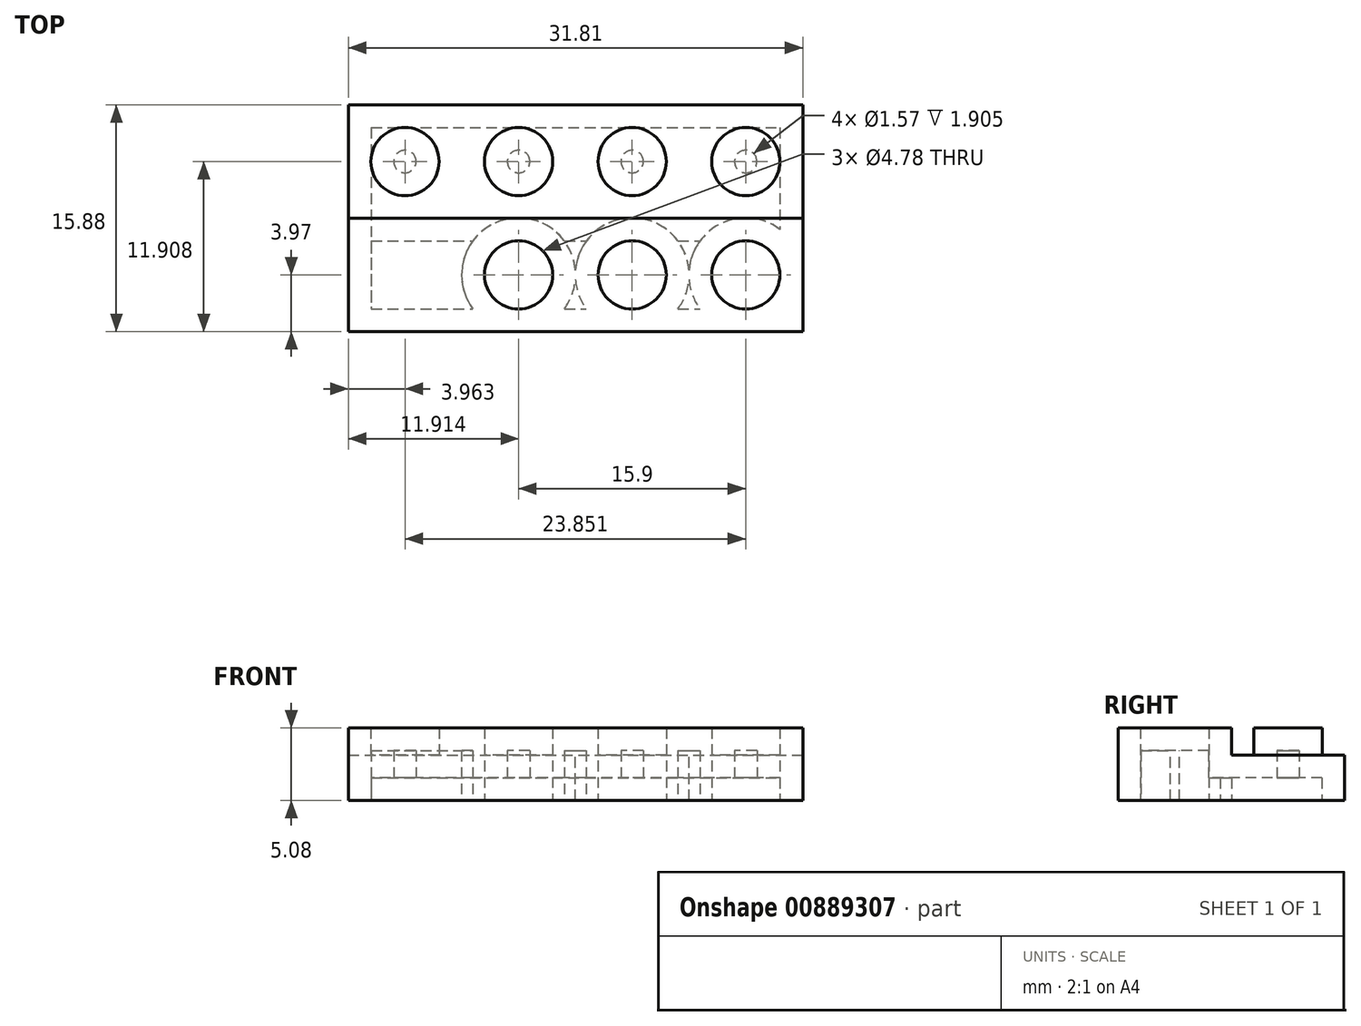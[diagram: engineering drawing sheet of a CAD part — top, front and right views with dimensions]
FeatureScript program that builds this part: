
annotation { "Feature Type Name" : "Feature", "Feature Type Description" : "" }
export const myFeature = defineFeature(function(context is Context, id is Id, definition is map)
    precondition{}
    {
        {
            var Q0;
            Q0=qCreatedBy(makeId("Top.planeOp"),FACE);
            var sketch = newSketch(context, id + "F0", { "sketchPlane" : qUnion([Q0])});
            skLineSegment(sketch, "E0.bottom", {"start": v(-38.8, 8.6) * mm, "end": v(-7, 8.6) * mm});
            skLineSegment(sketch, "E0.top", {"start": v(-38.8, -7.28) * mm, "end": v(-7, -7.28) * mm});
            skLineSegment(sketch, "E0.left", {"start": v(-38.8, 8.6) * mm, "end": v(-38.8, -7.28) * mm});
            skLineSegment(sketch, "E0.right", {"start": v(-7, 8.6) * mm, "end": v(-7, -7.28) * mm});
            skLineSegment(sketch, "E1", {"start": v(-38.8, 0.66) * mm, "end": v(-7, 0.66) * mm});
            skLineSegment(sketch, "E2", {"start": v(-7, 8.6) * mm, "end": v(-7, 0.66) * mm});
            skLineSegment(sketch, "E3", {"start": v(-7, 0.66) * mm, "end": v(-7, -7.28) * mm});
            skLineSegment(sketch, "E4", {"start": v(-38.8, 8.6) * mm, "end": v(-38.8, 0.66) * mm});
            skLineSegment(sketch, "E5", {"start": v(-38.8, -7.28) * mm, "end": v(-38.8, 0.66) * mm});
            skLineSegment(sketch, "E6", {"start": v(-7, -3.31) * mm, "end": v(-38.8, -3.31) * mm});
            skLineSegment(sketch, "E7", {"start": v(-38.8, -3.31) * mm, "end": v(-38.8, 4.63) * mm});
            skLineSegment(sketch, "E8", {"start": v(-38.8, 4.63) * mm, "end": v(-7, 4.63) * mm});
            skCircle(sketch, "E9", {"center": v(-34.85, 4.63) * mm, "radius": 2.39 * mm});
            skCircle(sketch, "E10.1.0.0", {"center": v(-26.9, 4.63) * mm, "radius": 2.39 * mm});
            skCircle(sketch, "E10.2.0.0", {"center": v(-18.95, 4.63) * mm, "radius": 2.39 * mm});
            skCircle(sketch, "E10.3.0.0", {"center": v(-11, 4.63) * mm, "radius": 2.39 * mm});
            skLineSegment(sketch, "E10.direction1", {"start": v(-34.85, 4.63) * mm, "end": v(-26.9, 4.63) * mm, "construction": true});
            skCircle(sketch, "E11.MirrorC", {"center": v(-34.85, -3.31) * mm, "radius": 2.39 * mm});
            skCircle(sketch, "E12.MirrorC", {"center": v(-26.9, -3.31) * mm, "radius": 2.39 * mm});
            skCircle(sketch, "E13.MirrorC", {"center": v(-18.95, -3.31) * mm, "radius": 2.39 * mm});
            skCircle(sketch, "E14.MirrorC", {"center": v(-11, -3.31) * mm, "radius": 2.39 * mm});
            skSolve(sketch);
        }
        {
            var Q0;
            {var subQ8=sQuery(id+"F0.wireOp",EDGE,"E0.bottom");Q0=makeQuery(id+"F0.imprint","IMPRINT",FACE,{"disambiguationData":[TD([[makeQuery(id+"F0.imprint","IMPRINT",EDGE,{"derivedFrom":subQ8}),-1.0]])]});}
            var Q1;
            {var subQ12=sQuery(id+"F0.wireOp",EDGE,"E1");Q1=makeQuery(id+"F0.imprint","IMPRINT",FACE,{"disambiguationData":[TD([[makeQuery(id+"F0.imprint","IMPRINT",EDGE,{"derivedFrom":subQ12}),1.0]])]});}
            var Q2;
            {var subQ12=sQuery(id+"F0.wireOp",EDGE,"E0.top");Q2=makeQuery(id+"F0.imprint","IMPRINT",FACE,{"disambiguationData":[TD([[makeQuery(id+"F0.imprint","IMPRINT",EDGE,{"derivedFrom":subQ12}),1.0]])]});}
            var Q3;
            {var subQ8=sQuery(id+"F0.wireOp",EDGE,"E1");Q3=makeQuery(id+"F0.imprint","IMPRINT",FACE,{"disambiguationData":[TD([[makeQuery(id+"F0.imprint","IMPRINT",EDGE,{"derivedFrom":subQ8}),-1.0]])]});}
            extrude(context, id + "F1", {"entities" : qUnion([Q0, Q1, Q2, Q3]), "depth" : 3.17 * mm, "offsetDistance" : 25.4 * mm});
        }
        {
            var Q0;
            {var subQ0=sQuery(id+"F0.wireOp",EDGE,"E9");var subQ1=sQuery(id+"F0.wireOp",EDGE,"E8");var subQ2=makeQuery(id+"F0.imprint","INTERSECT",VERTEX,{"disambiguationData":[OD(0.0)],"derivedFrom":[subQ1,subQ0]});Q0=makeQuery(id+"F0.imprint","IMPRINT",FACE,{"disambiguationData":[TD([[makeQuery(id+"F0.imprint","IMPRINT",EDGE,{"disambiguationData":[TD([[subQ2,-1.0]])],"derivedFrom":subQ1}),-1.0]])]});}
            var Q1;
            {var subQ0=sQuery(id+"F0.wireOp",EDGE,"E9");var subQ1=sQuery(id+"F0.wireOp",EDGE,"E8");var subQ2=makeQuery(id+"F0.imprint","INTERSECT",VERTEX,{"disambiguationData":[OD(0.0)],"derivedFrom":[subQ1,subQ0]});Q1=makeQuery(id+"F0.imprint","IMPRINT",FACE,{"disambiguationData":[TD([[makeQuery(id+"F0.imprint","IMPRINT",EDGE,{"disambiguationData":[TD([[subQ2,-1.0]])],"derivedFrom":subQ1}),1.0]])]});}
            var Q2;
            {var subQ0=sQuery(id+"F0.wireOp",EDGE,"E11.MirrorC");var subQ1=sQuery(id+"F0.wireOp",EDGE,"E6");var subQ2=makeQuery(id+"F0.imprint","INTERSECT",VERTEX,{"disambiguationData":[OD(0.0)],"derivedFrom":[subQ1,subQ0]});Q2=makeQuery(id+"F0.imprint","IMPRINT",FACE,{"disambiguationData":[TD([[makeQuery(id+"F0.imprint","IMPRINT",EDGE,{"disambiguationData":[TD([[subQ2,-1.0]])],"derivedFrom":subQ1}),-1.0]])]});}
            var Q3;
            {var subQ0=sQuery(id+"F0.wireOp",EDGE,"E11.MirrorC");var subQ1=sQuery(id+"F0.wireOp",EDGE,"E6");var subQ2=makeQuery(id+"F0.imprint","INTERSECT",VERTEX,{"disambiguationData":[OD(0.0)],"derivedFrom":[subQ1,subQ0]});Q3=makeQuery(id+"F0.imprint","IMPRINT",FACE,{"disambiguationData":[TD([[makeQuery(id+"F0.imprint","IMPRINT",EDGE,{"disambiguationData":[TD([[subQ2,-1.0]])],"derivedFrom":subQ1}),1.0]])]});}
            var Q4;
            {var subQ0=sQuery(id+"F0.wireOp",EDGE,"E12.MirrorC");var subQ1=sQuery(id+"F0.wireOp",EDGE,"E6");var subQ2=makeQuery(id+"F0.imprint","INTERSECT",VERTEX,{"disambiguationData":[OD(0.0)],"derivedFrom":[subQ1,subQ0]});Q4=makeQuery(id+"F0.imprint","IMPRINT",FACE,{"disambiguationData":[TD([[makeQuery(id+"F0.imprint","IMPRINT",EDGE,{"disambiguationData":[TD([[subQ2,-1.0]])],"derivedFrom":subQ1}),1.0]])]});}
            var Q5;
            {var subQ0=sQuery(id+"F0.wireOp",EDGE,"E12.MirrorC");var subQ1=sQuery(id+"F0.wireOp",EDGE,"E6");var subQ2=makeQuery(id+"F0.imprint","INTERSECT",VERTEX,{"disambiguationData":[OD(0.0)],"derivedFrom":[subQ1,subQ0]});Q5=makeQuery(id+"F0.imprint","IMPRINT",FACE,{"disambiguationData":[TD([[makeQuery(id+"F0.imprint","IMPRINT",EDGE,{"disambiguationData":[TD([[subQ2,-1.0]])],"derivedFrom":subQ1}),-1.0]])]});}
            var Q6;
            {var subQ0=sQuery(id+"F0.wireOp",EDGE,"E10.1.0.0");var subQ1=sQuery(id+"F0.wireOp",EDGE,"E8");var subQ2=makeQuery(id+"F0.imprint","INTERSECT",VERTEX,{"disambiguationData":[OD(0.0)],"derivedFrom":[subQ1,subQ0]});Q6=makeQuery(id+"F0.imprint","IMPRINT",FACE,{"disambiguationData":[TD([[makeQuery(id+"F0.imprint","IMPRINT",EDGE,{"disambiguationData":[TD([[subQ2,-1.0]])],"derivedFrom":subQ1}),-1.0]])]});}
            var Q7;
            {var subQ0=sQuery(id+"F0.wireOp",EDGE,"E10.1.0.0");var subQ1=sQuery(id+"F0.wireOp",EDGE,"E8");var subQ2=makeQuery(id+"F0.imprint","INTERSECT",VERTEX,{"disambiguationData":[OD(0.0)],"derivedFrom":[subQ1,subQ0]});Q7=makeQuery(id+"F0.imprint","IMPRINT",FACE,{"disambiguationData":[TD([[makeQuery(id+"F0.imprint","IMPRINT",EDGE,{"disambiguationData":[TD([[subQ2,-1.0]])],"derivedFrom":subQ1}),1.0]])]});}
            var Q8;
            {var subQ0=sQuery(id+"F0.wireOp",EDGE,"E13.MirrorC");var subQ1=sQuery(id+"F0.wireOp",EDGE,"E6");var subQ2=makeQuery(id+"F0.imprint","INTERSECT",VERTEX,{"disambiguationData":[OD(0.0)],"derivedFrom":[subQ1,subQ0]});Q8=makeQuery(id+"F0.imprint","IMPRINT",FACE,{"disambiguationData":[TD([[makeQuery(id+"F0.imprint","IMPRINT",EDGE,{"disambiguationData":[TD([[subQ2,-1.0]])],"derivedFrom":subQ1}),1.0]])]});}
            var Q9;
            {var subQ0=sQuery(id+"F0.wireOp",EDGE,"E13.MirrorC");var subQ1=sQuery(id+"F0.wireOp",EDGE,"E6");var subQ2=makeQuery(id+"F0.imprint","INTERSECT",VERTEX,{"disambiguationData":[OD(0.0)],"derivedFrom":[subQ1,subQ0]});Q9=makeQuery(id+"F0.imprint","IMPRINT",FACE,{"disambiguationData":[TD([[makeQuery(id+"F0.imprint","IMPRINT",EDGE,{"disambiguationData":[TD([[subQ2,-1.0]])],"derivedFrom":subQ1}),-1.0]])]});}
            var Q10;
            {var subQ0=sQuery(id+"F0.wireOp",EDGE,"E10.2.0.0");var subQ1=sQuery(id+"F0.wireOp",EDGE,"E8");var subQ2=makeQuery(id+"F0.imprint","INTERSECT",VERTEX,{"disambiguationData":[OD(0.0)],"derivedFrom":[subQ1,subQ0]});Q10=makeQuery(id+"F0.imprint","IMPRINT",FACE,{"disambiguationData":[TD([[makeQuery(id+"F0.imprint","IMPRINT",EDGE,{"disambiguationData":[TD([[subQ2,-1.0]])],"derivedFrom":subQ1}),1.0]])]});}
            var Q11;
            {var subQ0=sQuery(id+"F0.wireOp",EDGE,"E10.2.0.0");var subQ1=sQuery(id+"F0.wireOp",EDGE,"E8");var subQ2=makeQuery(id+"F0.imprint","INTERSECT",VERTEX,{"disambiguationData":[OD(0.0)],"derivedFrom":[subQ1,subQ0]});Q11=makeQuery(id+"F0.imprint","IMPRINT",FACE,{"disambiguationData":[TD([[makeQuery(id+"F0.imprint","IMPRINT",EDGE,{"disambiguationData":[TD([[subQ2,-1.0]])],"derivedFrom":subQ1}),-1.0]])]});}
            var Q12;
            {var subQ0=sQuery(id+"F0.wireOp",EDGE,"E14.MirrorC");var subQ1=sQuery(id+"F0.wireOp",EDGE,"E6");var subQ2=makeQuery(id+"F0.imprint","INTERSECT",VERTEX,{"disambiguationData":[OD(0.0)],"derivedFrom":[subQ1,subQ0]});Q12=makeQuery(id+"F0.imprint","IMPRINT",FACE,{"disambiguationData":[TD([[makeQuery(id+"F0.imprint","IMPRINT",EDGE,{"disambiguationData":[TD([[subQ2,-1.0]])],"derivedFrom":subQ1}),-1.0]])]});}
            var Q13;
            {var subQ0=sQuery(id+"F0.wireOp",EDGE,"E14.MirrorC");var subQ1=sQuery(id+"F0.wireOp",EDGE,"E6");var subQ2=makeQuery(id+"F0.imprint","INTERSECT",VERTEX,{"disambiguationData":[OD(0.0)],"derivedFrom":[subQ1,subQ0]});Q13=makeQuery(id+"F0.imprint","IMPRINT",FACE,{"disambiguationData":[TD([[makeQuery(id+"F0.imprint","IMPRINT",EDGE,{"disambiguationData":[TD([[subQ2,-1.0]])],"derivedFrom":subQ1}),1.0]])]});}
            var Q14;
            {var subQ0=sQuery(id+"F0.wireOp",EDGE,"E10.3.0.0");var subQ1=sQuery(id+"F0.wireOp",EDGE,"E8");var subQ2=makeQuery(id+"F0.imprint","INTERSECT",VERTEX,{"disambiguationData":[OD(0.0)],"derivedFrom":[subQ1,subQ0]});Q14=makeQuery(id+"F0.imprint","IMPRINT",FACE,{"disambiguationData":[TD([[makeQuery(id+"F0.imprint","IMPRINT",EDGE,{"disambiguationData":[TD([[subQ2,-1.0]])],"derivedFrom":subQ1}),-1.0]])]});}
            var Q15;
            {var subQ0=sQuery(id+"F0.wireOp",EDGE,"E10.3.0.0");var subQ1=sQuery(id+"F0.wireOp",EDGE,"E8");var subQ2=makeQuery(id+"F0.imprint","INTERSECT",VERTEX,{"disambiguationData":[OD(0.0)],"derivedFrom":[subQ1,subQ0]});Q15=makeQuery(id+"F0.imprint","IMPRINT",FACE,{"disambiguationData":[TD([[makeQuery(id+"F0.imprint","IMPRINT",EDGE,{"disambiguationData":[TD([[subQ2,-1.0]])],"derivedFrom":subQ1}),1.0]])]});}
            var Q16;
            Q16=qSketchRegion(id+"FatHljnlFBaRiWF_0",true);
            extrude(context, id + "F2", {"entities" : qUnion([Q0, Q1, Q2, Q3, Q4, Q5, Q6, Q7, Q8, Q9, Q10, Q11, Q12, Q13, Q14, Q15, Q16]), "operationType" : NewBodyOperationType.ADD, "depth" : 5.08 * mm, "offsetDistance" : 25.4 * mm});
        }
        {
            var Q0;
            {var subQ0=sQuery(id+"F0.wireOp",EDGE,"E14.MirrorC");var subQ1=sQuery(id+"F0.wireOp",EDGE,"E13.MirrorC");var subQ2=sQuery(id+"F0.wireOp",EDGE,"E12.MirrorC");var subQ3=sQuery(id+"F0.wireOp",EDGE,"E11.MirrorC");var subQ4=sQuery(id+"F0.wireOp",EDGE,"E10.3.0.0");var subQ5=sQuery(id+"F0.wireOp",EDGE,"E10.2.0.0");var subQ6=sQuery(id+"F0.wireOp",EDGE,"E10.1.0.0");var subQ7=sQuery(id+"F0.wireOp",EDGE,"E9");Q0=makeQuery(id+"F2.boolean.opBoolean","MERGE",FACE,{"derivedFrom":[makeQuery(id+"F1.opExtrude","CAP_FACE",FACE,{"disambiguationData":[OSD([sQuery(id+"F0.wireOp",EDGE,"E0.bottom"),sQuery(id+"F0.wireOp",EDGE,"E0.top"),sQuery(id+"F0.wireOp",EDGE,"E2"),sQuery(id+"F0.wireOp",EDGE,"E3"),sQuery(id+"F0.wireOp",EDGE,"E4"),sQuery(id+"F0.wireOp",EDGE,"E5"),sQuery(id+"F0.wireOp",EDGE,"E7"),subQ7,subQ6,subQ5,subQ4,subQ3,subQ2,subQ1,subQ0])],"isStart":true}),makeQuery(id+"F2.opExtrude","CAP_FACE",FACE,{"disambiguationData":[OSD([subQ7])],"isStart":true}),makeQuery(id+"F2.opExtrude","CAP_FACE",FACE,{"disambiguationData":[OSD([subQ6])],"isStart":true}),makeQuery(id+"F2.opExtrude","CAP_FACE",FACE,{"disambiguationData":[OSD([subQ5])],"isStart":true}),makeQuery(id+"F2.opExtrude","CAP_FACE",FACE,{"disambiguationData":[OSD([subQ4])],"isStart":true}),makeQuery(id+"F2.opExtrude","CAP_FACE",FACE,{"disambiguationData":[OSD([subQ3])],"isStart":true}),makeQuery(id+"F2.opExtrude","CAP_FACE",FACE,{"disambiguationData":[OSD([subQ2])],"isStart":true}),makeQuery(id+"F2.opExtrude","CAP_FACE",FACE,{"disambiguationData":[OSD([subQ1])],"isStart":true}),makeQuery(id+"F2.opExtrude","CAP_FACE",FACE,{"disambiguationData":[OSD([subQ0])],"isStart":true})]});}
            shell(context, id + "F3", {"entities" : qUnion([Q0]), "thickness" : 1.6 * mm});
        }
    });
